# Revit family: Riva 350
name_source: partatom
category: Lighting Fixtures
units: mm (PartAtom-declared; Revit-internal decimal feet)

## family parameters
Always vertical = Yes
Cut with Voids When Loaded = No
Host = Wall
Light Source = No
OmniClass Number = 23.80.70.00
OmniClass Title = Lighting
Part Type = Normal
Room Calculation Point = No
Round Connector Dimension = Use Diameter
Shared = No

## types (2) — shared parameters
Main Material = Metal - Steel
Manufacturer = Astro Lighting Ltd
Product Location = Bathroom
URL = www.astrolighting.com
zero-valued in all types: Default Elevation

## per-type parameters (varying)
| type | ADA compliant | Dimmable | Dimming Method | Driver Included | Driver Required | Electrical Class | Lamp | Length of Cable Supplied | Light Source Fixed | Location rating | Main Finish | Power (Watts) | Product Code | Product Name | Product SKU |
| CE | Not Applicable | Lamp Dependent | Lamp Dependent | Not Applicable | Not Applicable | 2 | 1x 60W max E27 es | Not Applicable | Replaceable | IP44 | Various | Lamp Dependent | 0 | Riva 350 | 1214001 |
| ETL | NO |  |  |  | No | 0 |  |  |  | DAMP |  |  | 1234 |  | 1234001 |

## geometry (parser evidence)
native form markers: Sweep x3
no freeform markers — native parametric forms only
